# Revit family: GR_Адаптер линейный_Муфта(n)_PV-КСД-У_О_R21
name_source: partatom
category: Соединительные детали воздуховодов
units: mm (PartAtom-declared; Revit-internal decimal feet)

## family parameters
Всегда вертикально = Да
Заголовок OmniClass = Metal Ducts
На основе рабочей плоскости = Нет
Номер OmniClass = 23.75.70.14.31
Общий = Нет
При загрузке вырезать с полостями = Нет
Размер круглого соединителя = Использовать диаметр
Тип детали = Мультипорт

## types (15) — shared parameters
ADSK_URL страницы изделия = https://grilles.ru
ADSK_Версия Revit = 2021
ADSK_Единица измерения = шт.
ADSK_Завод-изготовитель = ООО "ВЕНТРЕШЕТКИКОМ"
ADSK_Код изделия = 002092
ADSK_Количество = 1
ADSK_Материал = ADSK_Оцинкованная сталь
ADSK_Наименование = PV-КСД-У-О, адаптер вентиляционной решётки радиальный
Изготовитель = ООО "ВЕНТРЕШЕТКИКОМ"
Корпус_Металл_Толщина = 1 мм
Муфта_Металл_Толщина = 1 мм
zero-valued in all types: Отметка по умолчанию

## per-type parameters (varying)
| type | Корпус_Высота | Корпус_Длина | Решетка_отступ | Решётка_Высота |
| PV-КСД-У-О 1-20 | 130 мм | 170 мм | 25 мм | 48 мм |
| PV-КСД-У-О 1-30 | 130 мм | 175 мм | 30 мм | 58 мм |
| PV-КСД-У-О 1-40 | 130 мм | 180 мм | 35 мм | 68 мм |
| PV-КСД-У-О 1-50 | 130 мм | 185 мм | 40 мм | 78 мм |
| PV-КСД-У-О 1-60 | 170 мм | 190 мм | 45 мм | 88 мм |
| PV-КСД-У-О 1-70 | 170 мм | 195 мм | 50 мм | 98 мм |
| PV-КСД-У-О 2-20 | 130 мм | 215 мм | 49 мм | 95 мм |
| PV-КСД-У-О 2-25 | 130 мм | 225 мм | 54 мм | 105 мм |
| PV-КСД-У-О 2-30 | 130 мм | 235 мм | 59 мм | 115 мм |
| PV-КСД-У-О 3-20 | 130 мм | 265 мм | 72 мм | 142 мм |
| PV-КСД-У-О 3-25 | 130 мм | 280 мм | 80 мм | 157 мм |
| PV-КСД-У-О 3-30 | 130 мм | 295 мм | 87 мм | 172 мм |
| PV-КСД-У-О 4-20 | 170 мм | 310 мм | 96 мм | 189 мм |
| PV-КСД-У-О 4-25 | 170 мм | 330 мм | 106 мм | 209 мм |
| PV-КСД-У-О 4-30 | 170 мм | 350 мм | 116 мм | 229 мм |

note: column(s) folded — value = type name in every type: ADSK_Марка
